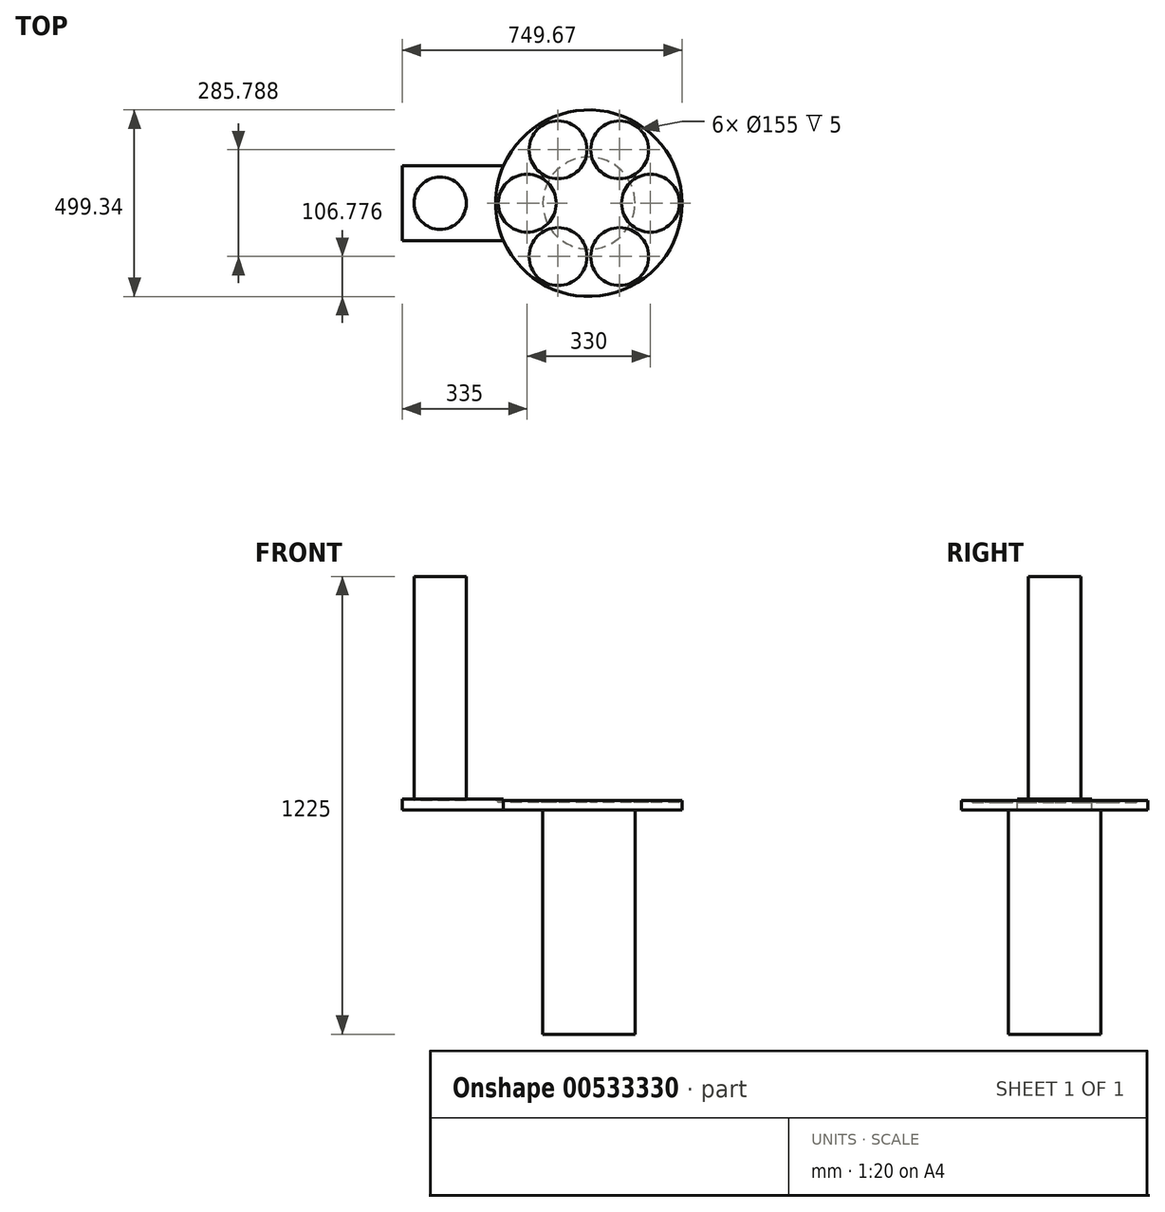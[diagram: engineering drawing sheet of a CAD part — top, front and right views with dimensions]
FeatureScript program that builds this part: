
annotation { "Feature Type Name" : "Feature", "Feature Type Description" : "" }
export const myFeature = defineFeature(function(context is Context, id is Id, definition is map)
    precondition{}
    {
        {
            var Q0;
            Q0=qCreatedBy(makeId("Top.planeOp"),FACE);
            var sketch = newSketch(context, id + "F0", { "sketchPlane" : qUnion([Q0])});
            skCircle(sketch, "E0", {"center": v(-165, 0) * mm, "radius": 77.5 * mm});
            skCircle(sketch, "E1.1.0", {"center": v(-82.5, -142.9) * mm, "radius": 77.5 * mm});
            skCircle(sketch, "E1.2.0", {"center": v(82.5, -142.9) * mm, "radius": 77.5 * mm});
            skCircle(sketch, "E1.3.0", {"center": v(165, 0) * mm, "radius": 77.5 * mm});
            skCircle(sketch, "E1.4.0", {"center": v(82.5, 142.9) * mm, "radius": 77.5 * mm});
            skCircle(sketch, "E1.5.0", {"center": v(-82.5, 142.9) * mm, "radius": 77.5 * mm});
            skPoint(sketch, "E1.center", {"position": v(0, 0) * mm});
            skCircle(sketch, "E2", {"center": v(0, 0) * mm, "radius": 249.67 * mm});
            skSolve(sketch);
        }
        {
            var Q0;
            Q0=makeQuery(id+"F0.imprint","IMPRINT",FACE,{"disambiguationData":[TD([[makeQuery(id+"F0.imprint","IMPRINT",EDGE,{"derivedFrom":sQuery(id+"F0.wireOp",EDGE,"E0")}),-1.0]])]});
            var Q1;
            Q1=makeQuery(id+"F0.imprint","IMPRINT",FACE,{"disambiguationData":[TD([[makeQuery(id+"F0.imprint","IMPRINT",EDGE,{"derivedFrom":sQuery(id+"F0.wireOp",EDGE,"E1.5.0")}),1.0]])]});
            var Q2;
            Q2=makeQuery(id+"F0.imprint","IMPRINT",FACE,{"disambiguationData":[TD([[makeQuery(id+"F0.imprint","IMPRINT",EDGE,{"derivedFrom":sQuery(id+"F0.wireOp",EDGE,"E1.4.0")}),1.0]])]});
            var Q3;
            Q3=makeQuery(id+"F0.imprint","IMPRINT",FACE,{"disambiguationData":[TD([[makeQuery(id+"F0.imprint","IMPRINT",EDGE,{"derivedFrom":sQuery(id+"F0.wireOp",EDGE,"E1.3.0")}),1.0]])]});
            var Q4;
            Q4=makeQuery(id+"F0.imprint","IMPRINT",FACE,{"disambiguationData":[TD([[makeQuery(id+"F0.imprint","IMPRINT",EDGE,{"derivedFrom":sQuery(id+"F0.wireOp",EDGE,"E0")}),1.0]])]});
            var Q5;
            Q5=makeQuery(id+"F0.imprint","IMPRINT",FACE,{"disambiguationData":[TD([[makeQuery(id+"F0.imprint","IMPRINT",EDGE,{"derivedFrom":sQuery(id+"F0.wireOp",EDGE,"E1.1.0")}),1.0]])]});
            var Q6;
            Q6=makeQuery(id+"F0.imprint","IMPRINT",FACE,{"disambiguationData":[TD([[makeQuery(id+"F0.imprint","IMPRINT",EDGE,{"derivedFrom":sQuery(id+"F0.wireOp",EDGE,"E1.2.0")}),1.0]])]});
            extrude(context, id + "F1", {"entities" : qUnion([Q0, Q1, Q2, Q3, Q4, Q5, Q6]), "oppositeDirection" : true, "depth" : 25 * mm, "offsetDistance" : 25 * mm});
        }
        {
            var Q0;
            Q0=makeQuery(id+"F0.imprint","IMPRINT",FACE,{"disambiguationData":[TD([[makeQuery(id+"F0.imprint","IMPRINT",EDGE,{"derivedFrom":sQuery(id+"F0.wireOp",EDGE,"E1.5.0")}),1.0]])]});
            var Q1;
            Q1=makeQuery(id+"F0.imprint","IMPRINT",FACE,{"disambiguationData":[TD([[makeQuery(id+"F0.imprint","IMPRINT",EDGE,{"derivedFrom":sQuery(id+"F0.wireOp",EDGE,"E1.4.0")}),1.0]])]});
            var Q2;
            Q2=makeQuery(id+"F0.imprint","IMPRINT",FACE,{"disambiguationData":[TD([[makeQuery(id+"F0.imprint","IMPRINT",EDGE,{"derivedFrom":sQuery(id+"F0.wireOp",EDGE,"E1.3.0")}),1.0]])]});
            var Q3;
            Q3=makeQuery(id+"F0.imprint","IMPRINT",FACE,{"disambiguationData":[TD([[makeQuery(id+"F0.imprint","IMPRINT",EDGE,{"derivedFrom":sQuery(id+"F0.wireOp",EDGE,"E1.2.0")}),1.0]])]});
            var Q4;
            Q4=makeQuery(id+"F0.imprint","IMPRINT",FACE,{"disambiguationData":[TD([[makeQuery(id+"F0.imprint","IMPRINT",EDGE,{"derivedFrom":sQuery(id+"F0.wireOp",EDGE,"E1.1.0")}),1.0]])]});
            var Q5;
            Q5=makeQuery(id+"F0.imprint","IMPRINT",FACE,{"disambiguationData":[TD([[makeQuery(id+"F0.imprint","IMPRINT",EDGE,{"derivedFrom":sQuery(id+"F0.wireOp",EDGE,"E0")}),1.0]])]});
            extrude(context, id + "F2", {"entities" : qUnion([Q0, Q1, Q2, Q3, Q4, Q5]), "operationType" : NewBodyOperationType.REMOVE, "oppositeDirection" : true, "depth" : 5 * mm, "offsetDistance" : 25 * mm});
        }
        {
            var Q0;
            Q0=makeQuery(id+"F0.imprint","IMPRINT",FACE,{"disambiguationData":[TD([[makeQuery(id+"F0.imprint","IMPRINT",EDGE,{"derivedFrom":sQuery(id+"F0.wireOp",EDGE,"E0")}),-1.0]])]});
            var sketch = newSketch(context, id + "F3", { "sketchPlane" : qUnion([Q0])});
            skCircle(sketch, "E3.0", {"center": v(0, 0) * mm, "radius": 249.67 * mm});
            skLineSegment(sketch, "E4", {"start": v(-228.77, 100) * mm, "end": v(-500, 100) * mm});
            skLineSegment(sketch, "E5", {"start": v(-500, 100) * mm, "end": v(-500, -100) * mm});
            skLineSegment(sketch, "E6", {"start": v(-500, -100) * mm, "end": v(-228.77, -100) * mm});
            skPoint(sketch, "E7.first.point", {"position": v(-424.39, 100) * mm});
            skPoint(sketch, "E7.second.point", {"position": v(-420.25, -100) * mm});
            skPoint(sketch, "E7.third.point", {"position": v(-500, 0) * mm});
            skCircle(sketch, "E8", {"center": v(-398.2, 0) * mm, "radius": 70 * mm});
            skSolve(sketch);
        }
        {
            var Q0;
            {var subQ1=sQuery(id+"F3.wireOp",EDGE,"E4");Q0=makeQuery(id+"F3.imprint","IMPRINT",FACE,{"disambiguationData":[TD([[makeQuery(id+"F3.imprint","IMPRINT",EDGE,{"derivedFrom":subQ1}),1.0]])]});}
            var Q1;
            Q1=makeQuery(id+"F3.imprint","IMPRINT",FACE,{"disambiguationData":[TD([[makeQuery(id+"F3.imprint","IMPRINT",EDGE,{"derivedFrom":sQuery(id+"F3.wireOp",EDGE,"E8")}),1.0]])]});
            extrude(context, id + "F4", {"entities" : qUnion([Q0, Q1]), "operationType" : NewBodyOperationType.ADD, "oppositeDirection" : true, "depth" : 25 * mm, "offsetDistance" : 25 * mm, "hasSecondDirection" : true, "secondDirectionOppositeDirection" : false, "secondDirectionDepth" : 5 * mm});
        }
        {
            var Q0;
            Q0=makeQuery(id+"F3.imprint","IMPRINT",FACE,{"disambiguationData":[TD([[makeQuery(id+"F3.imprint","IMPRINT",EDGE,{"derivedFrom":sQuery(id+"F3.wireOp",EDGE,"E8")}),1.0]])]});
            extrude(context, id + "F5", {"entities" : qUnion([Q0]), "depth" : 600 * mm, "offsetDistance" : 25 * mm});
        }
        {
            var Q0;
            Q0=makeQuery(id+"F4.boolean.opBoolean","MERGE",FACE,{"derivedFrom":[makeQuery(id+"F1.opExtrude","CAP_FACE",FACE,{"disambiguationData":[OSD([sQuery(id+"F0.wireOp",EDGE,"E2")])],"isStart":false}),makeQuery(id+"F4.opExtrude","CAP_FACE",FACE,{"disambiguationData":[OSD([sQuery(id+"F3.wireOp",EDGE,"E3.0"),sQuery(id+"F3.wireOp",EDGE,"E4"),sQuery(id+"F3.wireOp",EDGE,"E5"),sQuery(id+"F3.wireOp",EDGE,"E6")])],"isStart":false})]});
            var sketch = newSketch(context, id + "F6", { "sketchPlane" : qUnion([Q0])});
            skCircle(sketch, "E9", {"center": v(0, 0) * mm, "radius": 123.34 * mm});
            skSolve(sketch);
        }
        {
            var Q0;
            Q0=makeQuery(id+"F6.imprint","IMPRINT",FACE,{"disambiguationData":[TD([[makeQuery(id+"F6.imprint","IMPRINT",EDGE,{"derivedFrom":sQuery(id+"F6.wireOp",EDGE,"E9")}),1.0]])]});
            extrude(context, id + "F7", {"entities" : qUnion([Q0]), "operationType" : NewBodyOperationType.ADD, "depth" : 600 * mm, "offsetDistance" : 25 * mm});
        }
    });
